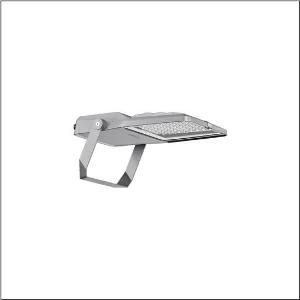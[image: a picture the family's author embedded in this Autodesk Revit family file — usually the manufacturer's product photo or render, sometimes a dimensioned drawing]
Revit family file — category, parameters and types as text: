
# Revit family: floodlight_fl_21_iq_mini___pl64_5xa7771c4e1a_d4bc
name_source: partatom
category: Lighting Fixtures
units: mm (PartAtom-declared; Revit-internal decimal feet)

## family parameters
Cut with Voids When Loaded = No
Host = Face
Light Source = No
Part Type = Normal
Room Calculation Point = No
Round Connector Dimension = Use Diameter
Shared = No

## types (1)
- --- (1 x LED, 12280 lm, 87.2 W, 4000K)
    Apparent Load = 87 VA
    CIE Flux Codes = 28 80 98 100 100
    Color Rendering = 70
    Color Temperature = 4000K
    Default Elevation = 1800 mm
    Description = Floodlight FL 21 iQ mini, floodlight, primary light control with lens, of PMMA, primary optical cover: protective disc, of toughened safety glass, transparent, light distribution: PL64, light emission: direct distribution, installation type: surface-mounted, LED, High Power LED, rated luminous flux: 12.280lm, luminous efficacy: 141lm/W, light colour: 740, colour temperature: 4000K, control: Auto-Match, Temp-Guard, Lumen-Switch, Night-Set, Smart-Wire, Light-Fading, Desk-Remote (wireless, voltage-free reading and setting of iQ features in the workshop via application-optimized NFC function/RFID function), optimised constant luminous flux control (CLO 2.0), with terminal, 6-pole, mains connection: 220..240V, AC, 50/60Hz, start of lifetime: 87W, end of service life: 92W, reduction: 40W, luminaire housing, of diecast aluminium, powder-coated, Siteco® metallic grey (DB 702S), corrosivity category C5 mid according to DIN EN ISO 12944, sealing non-destructively replaceable, mounting bracket, of steel, galvanised, powder-coated, Siteco® metallic grey (DB 702S), protection rating (complete): IP66, insulation class (complete): insulation class II (safety insulation), certification: CE, ENEC, VDE, protection symbol: D, impact resistance: IK08, permissible operating ambient temperature: -40..+40°C, permissible operating ambient temperature for outdoor applications: -40..+50°C, standard: DIN EN 12944, LABS conformity tested according to VDMA 24364:2018-05, packaging unit: 1 piece

Light Distribution: PL64
    Height = 70 mm
    Lamp = 1 x LED
    Lamp Light Flux = 12280 lm
    Lamp Power = 87.2 W
    Lamp count = 1
    Length = 485 mm
    Luminous efficacy = 141 lm/W
    Manufacturer = Siteco
    ModVariant = No
    Model = 5XA7771C4E1A
    Number of Poles = 1
    OnlyDefault = Yes
    Power Factor = 1
    Product Name = Floodlight FL 21 iQ mini | PL64
    Product group = floodlight | pylon annexe
    ProductGroupID = 6200
    Protection Class = Protection class II
    Protection Degree = IP 66
    RLX_Detail_Level = 1
    RLX_Emergency_Light_Flux = 0 lm
    RLX_Emergency_Type = 0
    RLX_Emergency_Type_DB = No
    RlxData = <blob elided: 96277 chars, md5=92061117>
    Socket = socket
    Standby Power = 0 W
    System Light Flux = 12280 lm
    System Power = 87 W
    Type Comments = factory setting: luminous flux: 100 % | dim-lin: 254 | 456 mA
    Type Image = l_1006845.jpg
    URL = http://relux.com
    VarID = @adj_098877
    Voltage = 0 V
    Weight = 0.00 kg
    Width = 337 mm

## geometry (parser evidence)
native form markers: Blend x4, Sweep x12
no freeform markers — native parametric forms only
